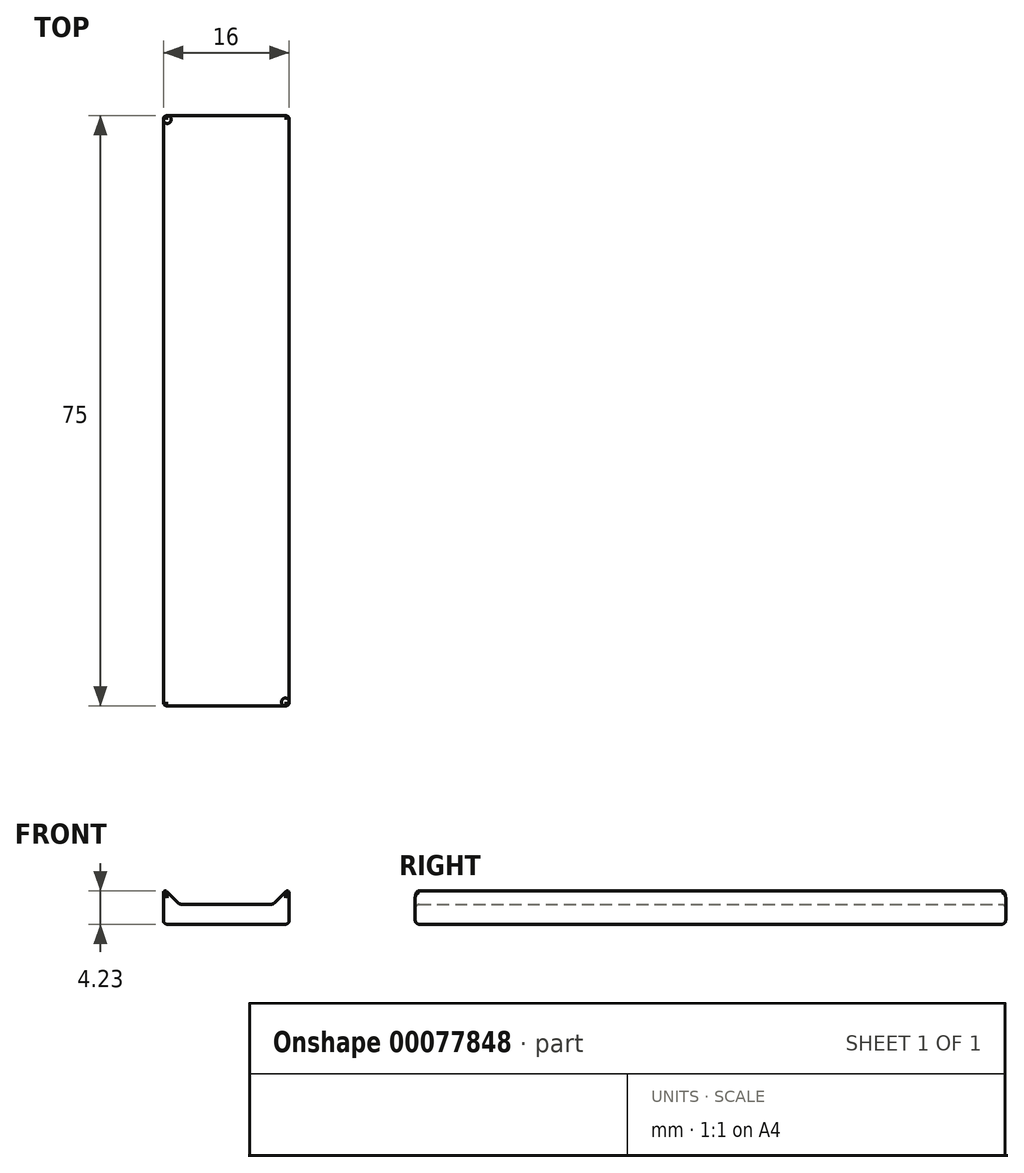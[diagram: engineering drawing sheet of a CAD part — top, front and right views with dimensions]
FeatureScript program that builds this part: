
annotation { "Feature Type Name" : "Feature", "Feature Type Description" : "" }
export const myFeature = defineFeature(function(context is Context, id is Id, definition is map)
    precondition{}
    {
        {
            var Q0;
            Q0=qCreatedBy(makeId("Front.planeOp"),FACE);
            var sketch = newSketch(context, id + "F0", { "sketchPlane" : qUnion([Q0])});
            skLineSegment(sketch, "E0", {"start": v(5.5, 0) * mm, "end": v(-5.5, 0) * mm});
            skLineSegment(sketch, "E1", {"start": v(-6.2, 0.3) * mm, "end": v(-7.57, 1.66) * mm});
            skLineSegment(sketch, "E2", {"start": v(-8, 1.48) * mm, "end": v(-8, -2) * mm});
            skLineSegment(sketch, "E3", {"start": v(-7.5, -2.5) * mm, "end": v(7.5, -2.5) * mm});
            skLineSegment(sketch, "E4", {"start": v(8, -2) * mm, "end": v(8, 1.48) * mm});
            skLineSegment(sketch, "E5", {"start": v(7.57, 1.66) * mm, "end": v(6.2, 0.3) * mm});
            skPoint(sketch, "E6.visualSharp", {"position": v(5.91, 0) * mm});
            skArc(sketch, "E6.filletArc", {"start": v(5.5, 0) * mm, "mid": v(5.88, 0.08) * mm, "end": v(6.2, 0.3) * mm});
            skPoint(sketch, "E7.visualSharp", {"position": v(-5.91, 0) * mm});
            skArc(sketch, "E7.filletArc", {"start": v(-6.2, 0.3) * mm, "mid": v(-5.88, 0.08) * mm, "end": v(-5.5, 0) * mm});
            skPoint(sketch, "E8.visualSharp", {"position": v(-8, 2.09) * mm});
            skArc(sketch, "E8.filletArc", {"start": v(-7.57, 1.66) * mm, "mid": v(-7.85, 1.71) * mm, "end": v(-8, 1.48) * mm});
            skPoint(sketch, "E9.visualSharp", {"position": v(8, 2.09) * mm});
            skArc(sketch, "E9.filletArc", {"start": v(8, 1.48) * mm, "mid": v(7.85, 1.71) * mm, "end": v(7.57, 1.66) * mm});
            skPoint(sketch, "E10", {"position": v(0, 0) * mm});
            skPoint(sketch, "E11.visualSharp", {"position": v(-8, -2.5) * mm});
            skArc(sketch, "E11.filletArc", {"start": v(-8, -2) * mm, "mid": v(-7.85, -2.35) * mm, "end": v(-7.5, -2.5) * mm});
            skPoint(sketch, "E12.visualSharp", {"position": v(8, -2.5) * mm});
            skArc(sketch, "E12.filletArc", {"start": v(7.5, -2.5) * mm, "mid": v(7.85, -2.35) * mm, "end": v(8, -2) * mm});
            skSolve(sketch);
        }
        {
            var Q0;
            Q0=makeQuery(id+"F0.imprint","IMPRINT",FACE,{"disambiguationData":[TD([[makeQuery(id+"F0.imprint","IMPRINT",EDGE,{"derivedFrom":sQuery(id+"F0.wireOp",EDGE,"E0")}),1.0]])]});
            extrude(context, id + "F1", {"entities" : qUnion([Q0]), "depth" : 75 * mm});
        }
        {
            var Q0;
            Q0=makeQuery(id+"F1.opExtrude","CAP_EDGE",EDGE,{"disambiguationData":[OSD([sQuery(id+"F0.wireOp",EDGE,"E0")])],"isStart":true});
            var Q1;
            Q1=makeQuery(id+"F1.opExtrude","CAP_EDGE",EDGE,{"disambiguationData":[OSD([sQuery(id+"F0.wireOp",EDGE,"E3")])],"isStart":false});
            fillet(context, id + "F2", {"entities" : qUnion([Q0, Q1]), "radius" : 0.5 * mm, "tangentPropagation" : true, "allowEdgeOverflow" : false});
        }
    });
